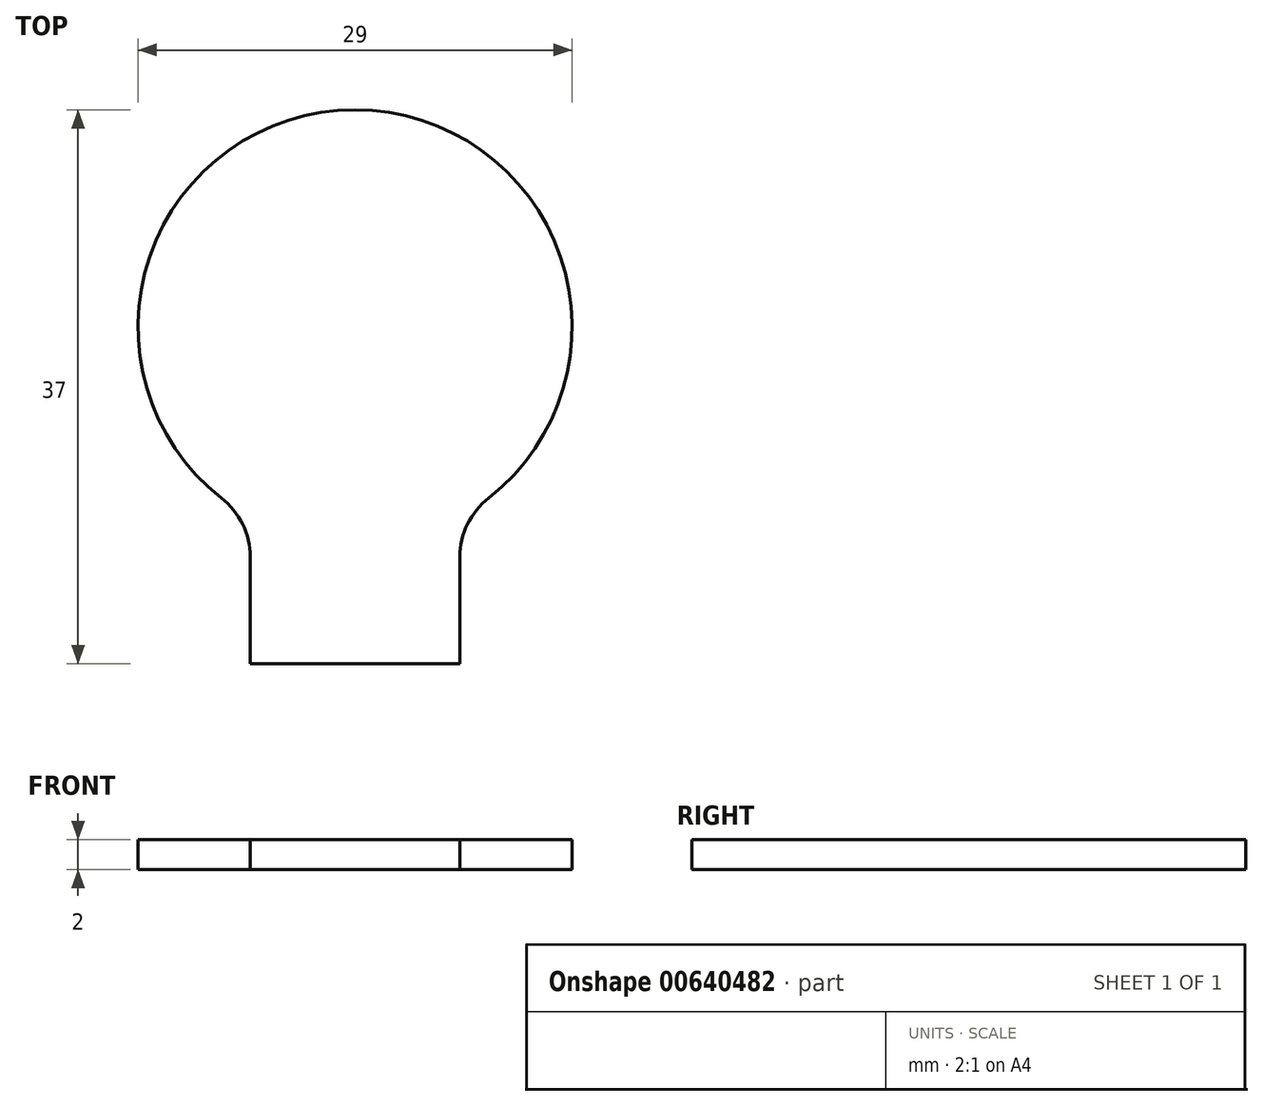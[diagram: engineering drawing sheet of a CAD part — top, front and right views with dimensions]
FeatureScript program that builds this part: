
annotation { "Feature Type Name" : "Feature", "Feature Type Description" : "" }
export const myFeature = defineFeature(function(context is Context, id is Id, definition is map)
    precondition{}
    {
        {
            var Q0;
            Q0=qCreatedBy(makeId("Top.planeOp"),FACE);
            var sketch = newSketch(context, id + "F0", { "sketchPlane" : qUnion([Q0])});
            skArc(sketch, "E0", {"start": v(7, -12.7) * mm, "mid": v(0, 14.5) * mm, "end": v(-7, -12.7) * mm});
            skLineSegment(sketch, "E1", {"start": v(0, 14.5) * mm, "end": v(0, -22.5) * mm});
            skLineSegment(sketch, "E2", {"start": v(0, -22.5) * mm, "end": v(7, -22.5) * mm});
            skLineSegment(sketch, "E3.MirrorCS", {"start": v(0, -22.5) * mm, "end": v(-7, -22.5) * mm});
            skLineSegment(sketch, "E4", {"start": v(7, -22.5) * mm, "end": v(7, -16.5) * mm});
            skLineSegment(sketch, "E5.MirrorCS", {"start": v(-7, -22.5) * mm, "end": v(-7, -16.5) * mm});
            skLineSegment(sketch, "E6", {"start": v(-7, -16.5) * mm, "end": v(-7, -12.7) * mm});
            skLineSegment(sketch, "E7", {"start": v(7, -16.5) * mm, "end": v(7, -12.7) * mm});
            skSolve(sketch);
        }
        {
            var Q0;
            Q0 = qSketchRegion(id + "F0", true);
            extrude(context, id + "F1", {"entities" : qUnion([Q0]), "depth" : 2 * mm, "offsetDistance" : 25 * mm});
        }
        {
            var Q0;
            Q0=makeQuery(id+"F1.opExtrude","SWEPT_EDGE",EDGE,{"disambiguationData":[OSD([sQuery(id+"F0.wireOp",EDGE,"E0"),sQuery(id+"F0.wireOp",EDGE,"E6")])]});
            fillet(context, id + "F2", {"entities" : qUnion([Q0]), "radius" : 5 * mm, "tangentPropagation" : true, "allowEdgeOverflow" : false});
        }
        {
            var Q0;
            Q0=makeQuery(id+"F1.opExtrude","SWEPT_EDGE",EDGE,{"disambiguationData":[OSD([sQuery(id+"F0.wireOp",EDGE,"E0"),sQuery(id+"F0.wireOp",EDGE,"E7")])]});
            fillet(context, id + "F3", {"entities" : qUnion([Q0]), "radius" : 5 * mm, "tangentPropagation" : true, "allowEdgeOverflow" : false});
        }
    });
